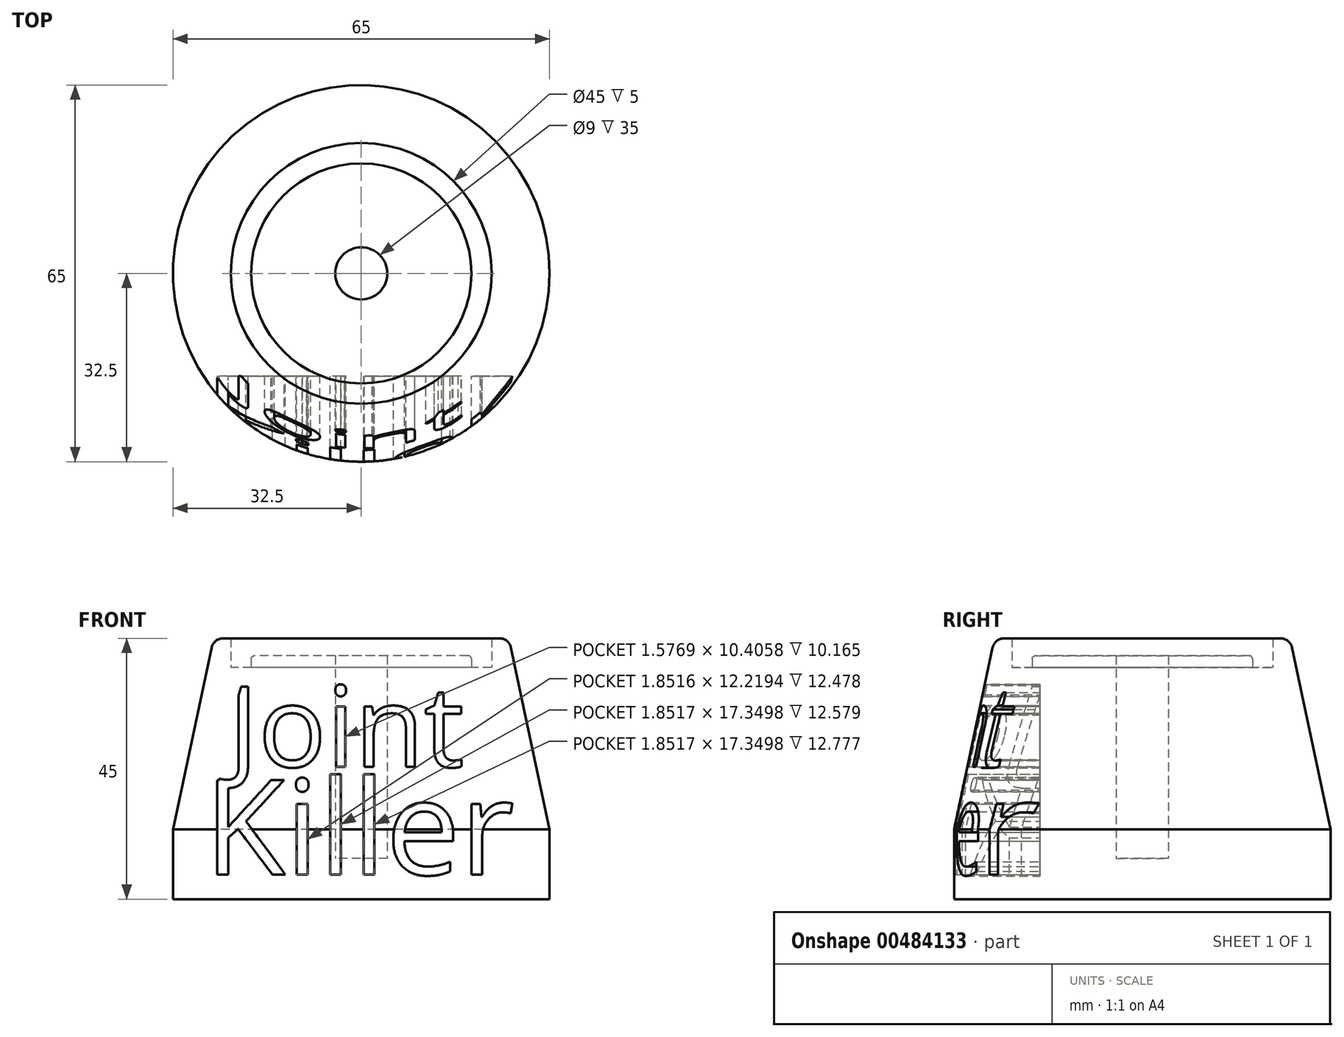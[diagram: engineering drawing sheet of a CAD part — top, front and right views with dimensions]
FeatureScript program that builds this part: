
annotation { "Feature Type Name" : "Feature", "Feature Type Description" : "" }
export const myFeature = defineFeature(function(context is Context, id is Id, definition is map)
    precondition{}
    {
        {
            var Q0;
            Q0=qCreatedBy(makeId("Top.planeOp"),FACE);
            var sketch = newSketch(context, id + "F0", { "sketchPlane" : qUnion([Q0])});
            skCircle(sketch, "E0", {"center": v(0, 0) * mm, "radius": 22.5 * mm});
            skCircle(sketch, "E1", {"center": v(0, 0) * mm, "radius": 19 * mm});
            skCircle(sketch, "E2", {"center": v(0, 0) * mm, "radius": 32.5 * mm});
            skCircle(sketch, "E3", {"center": v(0, 0) * mm, "radius": 4.5 * mm});
            skSolve(sketch);
        }
        {
            var Q0;
            Q0=qSketchRegion(id+"F0",true);
            extrude(context, id + "F1", {"entities" : qUnion([Q0]), "depth" : 4 * mm});
        }
        {
            var Q0;
            Q0=makeQuery(id+"F0.imprint","IMPRINT",FACE,{"disambiguationData":[TD([[makeQuery(id+"F0.imprint","IMPRINT",EDGE,{"derivedFrom":sQuery(id+"F0.wireOp",EDGE,"E0")}),-1.0]])]});
            extrude(context, id + "F2", {"entities" : qUnion([Q0]), "operationType" : NewBodyOperationType.ADD, "depth" : 45 * mm});
        }
        {
            var Q0;
            Q0=makeQuery(id+"F0.imprint","IMPRINT",FACE,{"disambiguationData":[TD([[makeQuery(id+"F0.imprint","IMPRINT",EDGE,{"derivedFrom":sQuery(id+"F0.wireOp",EDGE,"E0")}),1.0]])]});
            extrude(context, id + "F3", {"entities" : qUnion([Q0]), "operationType" : NewBodyOperationType.ADD, "depth" : 40 * mm});
        }
        {
            var Q0;
            Q0=makeQuery(id+"F0.imprint","IMPRINT",FACE,{"disambiguationData":[TD([[makeQuery(id+"F0.imprint","IMPRINT",EDGE,{"derivedFrom":sQuery(id+"F0.wireOp",EDGE,"E1")}),1.0]])]});
            extrude(context, id + "F4", {"entities" : qUnion([Q0]), "operationType" : NewBodyOperationType.ADD, "depth" : 42 * mm});
        }
        {
            var Q0;
            Q0=makeQuery(id+"F0.imprint","IMPRINT",FACE,{"disambiguationData":[TD([[makeQuery(id+"F0.imprint","IMPRINT",EDGE,{"derivedFrom":sQuery(id+"F0.wireOp",EDGE,"E3")}),1.0]])]});
            extrude(context, id + "F5", {"entities" : qUnion([Q0]), "operationType" : NewBodyOperationType.ADD, "depth" : 7 * mm});
        }
        {
            var Q0;
            Q0=makeQuery(id+"F2.opExtrude","CAP_EDGE",EDGE,{"disambiguationData":[OSD([sQuery(id+"F0.wireOp",EDGE,"E2")])],"isStart":false});
            chamfer(context, id + "F6", {"entities" : qUnion([Q0]), "chamferType" : ChamferType.OFFSET_ANGLE, "width" : 7 * mm, "oppositeDirection" : false, "angle" : 78 * degree, "tangentPropagation" : true});
        }
        {
            var Q0;
            {var subQ0=sQuery(id+"F0.wireOp",EDGE,"E2");Q0=makeQuery(id+"F6.opChamfer","BLEND_EDGE",EDGE,{"blendedFrom":[makeQuery(id+"F2.opExtrude","CAP_EDGE",EDGE,{"disambiguationData":[OSD([subQ0])],"isStart":false}),makeQuery(id+"F2.opExtrude","CAP_FACE",FACE,{"disambiguationData":[OSD([sQuery(id+"F0.wireOp",EDGE,"E0"),subQ0])],"isStart":false})],"blendedInto":[makeQuery(id+"F2.opExtrude","CAP_FACE",FACE,{"disambiguationData":[OSD([sQuery(id+"F0.wireOp",EDGE,"E0"),subQ0])],"isStart":false})]});}
            fillet(context, id + "F7", {"entities" : qUnion([Q0]), "radius" : 2 * mm, "tangentPropagation" : true, "allowEdgeOverflow" : false});
        }
        {
            var Q0;
            Q0=makeQuery(id+"F4.opExtrude","CAP_EDGE",EDGE,{"disambiguationData":[OSD([sQuery(id+"F0.wireOp",EDGE,"E1")])],"isStart":false});
            fillet(context, id + "F8", {"entities" : qUnion([Q0]), "radius" : 0.5 * mm, "tangentPropagation" : true, "allowEdgeOverflow" : false});
        }
        {
            var Q0;
            Q0=qCreatedBy(makeId("Front.planeOp"),FACE);
            var sketch = newSketch(context, id + "F9", { "sketchPlane" : qUnion([Q0])});
            skText(sketch, "E4", { "text": "Joint", "fontName": "OpenSans-Regular.ttf"});
            skText(sketch, "E5", { "text": "Killer", "fontName": "OpenSans-Regular.ttf"});
            const initialGuessF9  = {"E4": [-0.02296, 0.02282, 1, 0, 0.014], "E5": [-0.0271, 0.00422, 1, 0, 0.01644]};
            skSetInitialGuess(sketch, initialGuessF9);
            skSolve(sketch);
        }
        {
            var Q0;
            Q0 = qSketchRegion(id + "F9", true);
            extrude(context, id + "F10", {"entities" : qUnion([Q0]), "operationType" : NewBodyOperationType.REMOVE, "endBound" : BoundingType.THROUGH_ALL, "depth" : 85.2 * mm, "offsetDistance" : 25 * mm, "hasSecondDirection" : true, "secondDirectionOppositeDirection" : false, "secondDirectionDepth" : 17.7 * mm});
        }
    });
